# Revit family: 2015_Ventana_Alugom_ALG 65 Optima_1-Hoja_Practicable
name_source: partatom
category: Windows
revit_build: Autodesk Revit 2015 (Build: 20140223_1515(x64)
units: mm (PartAtom-declared; Revit-internal decimal feet)

## types (1)
- 800 mm x 1200 mm
    AcidificacionAtmosferica = 0
    AcidificacionAtmosfericaPorUnidad = 0
    Acristalamiento = Vidrio
    AguaConsumida = 0
    AguaConsumidaPorUnidad = 0
    Altura Máxima = 2500 mm  [stored 8.2021 ft]
    Altura Real = 1200 mm
    Altura de antepecho por defecto = 800 mm  [stored 2.62467 ft]
    AnchoMarco = 89 mm
    Anchura Máxima = 1700 mm  [stored 5.57743 ft]
    Anchura Real = 800 mm  [stored 2.62467 ft]
    Area = 960000 mm²
    Autor = Bimetica Parametric Design Services, S.L.
    Bimetica = http://www.bimetica.com
    CambioClimatico = 0
    CambioClimaticoPorUnidad = 0
    CerramientoExterior = Yes
    ConfiguracionPoliamidas = 350300 - 464700 - 464600 - 479900
    ControlHumos = Yes
    CosteEnergeticoKwh = 0
    CosteEnergeticoMj = 0 J
    CosteMantenimiento = 0
    Description = Ventana Practicable
    DesfaseExterior = 0 mm  [stored 0 ft]
    DesfaseInterior = 0 mm  [stored 0 ft]
    DestruccionCapaOzonoEstratosferica = 0
    DestruccionCapaOzonoEstratosfericaPorUnidad = 0
    Detalle Perfileria = Yes
    EmisionCO2 = 0
    EnergiaNoRenovableConsumida = 0
    EnergiaNoRenovableConsumidaPorUnidad = 0
    EnergiaPrimariaTotalConsumida = 0
    EnergiaPrimariaTotalConsumidaPorUnidad = 0
    EnergiaRenovableConsumida = 0
    EnergiaRenovableConsumidaPorUnidad = 0
    Eutrofizacion = 0
    EutrofizacionPorUnidad = 0
    FactorSolarModificado = 3000000
    FactorSombra = 0
    FaltaDeRecursos = 0
    FaltaDeRecursosPorUnidad = 0
    FechaEmisionElementoBIM = 02/09/2016
    FechaVencimientoElementoBIM = 02/09/2017
    FormacionFotoquimicaOzono = 0
    FormacionFotoquimicaOzonoPorUnidad = 0
    FraccionAreaAcristalamiento = 0.00%
    GrosorAcristalamiento = 39 mm  [stored 0.127953 ft]
    GrosorMarco = 72 mm  [stored 0.23622 ft]
    Height = 1200 mm
    InformacionTecnica = http://www.alugom.com
    Manija = Yes
    Manufacturer = Grupo Alugom
    Marco = Aluminio
    MasaSuperficialKgm2 = 0
    MasterformatCodigo = 08 51 13
    MasterformatTitulo = Aluminium Windows
    MateriaPrima = 0
    Model = ALG65 Óptima Practicable
    Motorizada = No
    OmniclassCodigo = 23.30.20.17.21.21
    OmniclassTitulo = Casment Window
    Operation = Practicable
    Perimetro = 4000
    Poliamida = Poliamida, Technoform Bautec, PA66 GF 25
    Practicable = Yes
    Proyección Apertura = Yes
    ReferenciaContacto = Alugom
    RepisaExterior = No
    RepisaInterior = No
    ResiduoInerte = 0
    ResiduoInertePorUnidad = 0
    ResiduoRadioactivo = 0
    ResiduoRadioactivoPorUnidad = 0
    ResiduosNoPeligrosos = 0
    ResiduosNoPeligrososPorUnidad = 0
    ResiduosPeligrosos = 0
    ResiduosPeligrososPorUnidad = 0
    SalidaEmergencia = Yes
    TelefonoContacto = 34 91 616 47 27
    TransmitanciaTermica = 0 W/(m²·K)
    Type Comments = Sistema de Ventana de 1 Hoja Rotura de Puente Térmico ALG65 Óptima Practicable.
    UNSPSCCodigo = 30171600
    UNSPSCTitulo = Windows
    URL = http://www.alugom.com
    URL Poliamida = http://www.technoform.es
    URL Poliamida - Catálogo = http://www.technoform.com
    URLProducto = http://www.alugom.com
    Uniclass2.0Codigo = "25-30"
    Uniclass2.0Titulo = "Door and window systems"
    VersionElementoBIM = 1.0
    Wall Closure = By host
    Width = 800 mm  [stored 2.62467 ft]
    Y𝑔 = 0.11
    𝐴𝑓 = 324644.76
    𝐴𝑔 = 635355.24
    𝑈𝑓 = 3.629
    𝑈𝑔 = 1.9
    𝑈𝑤 = 2.861357
    𝑙𝑔 = 3287.2

note: [stored X ft] marks values corroborated as IEEE doubles in the binary element streams (Revit-internal decimal feet)
